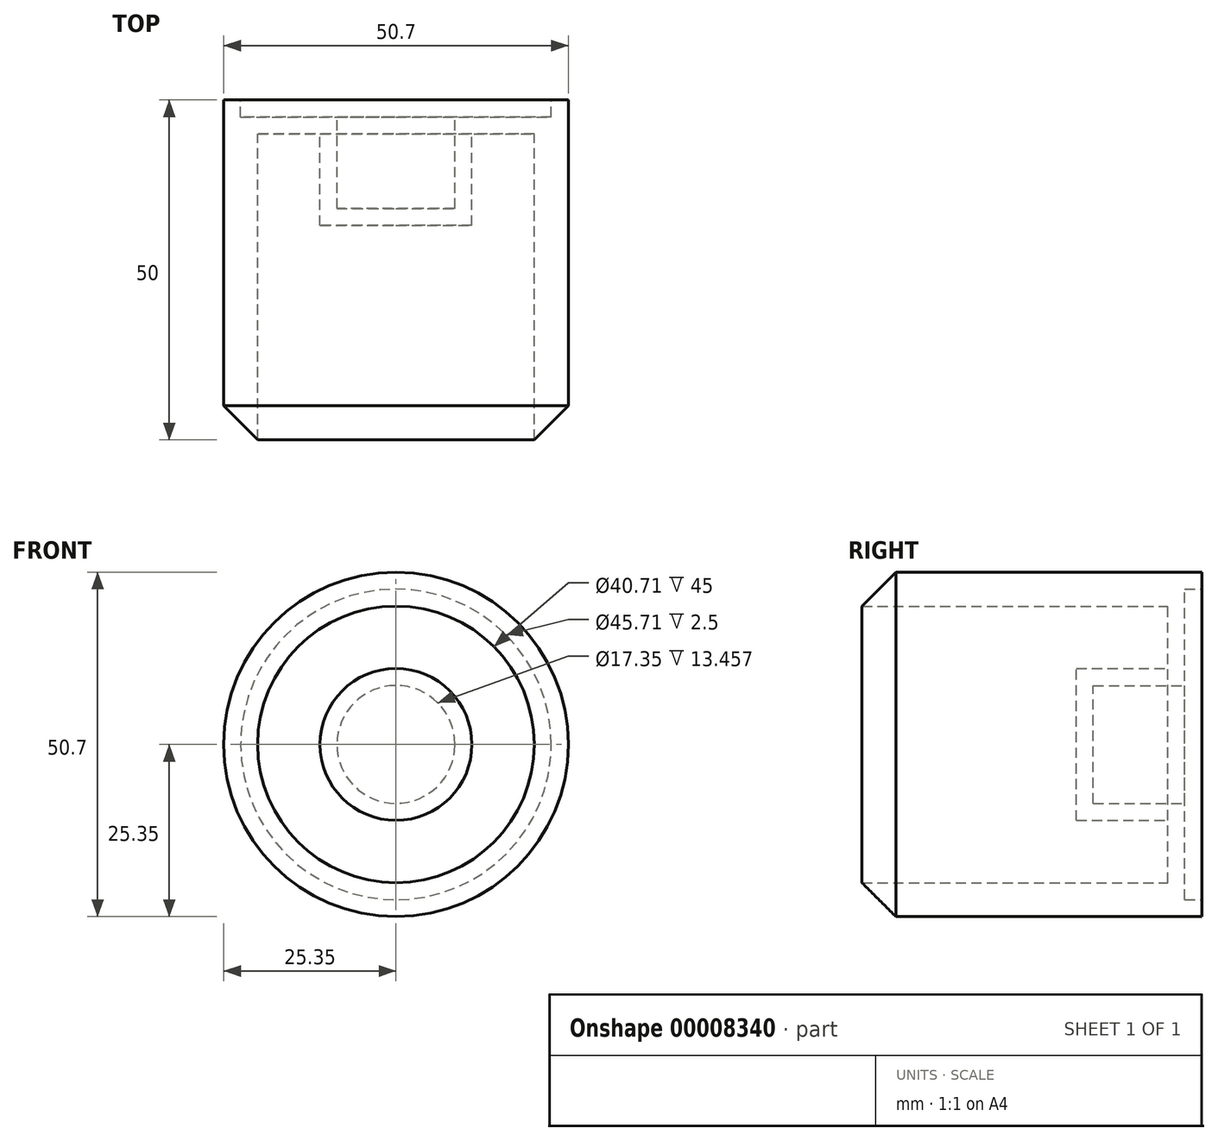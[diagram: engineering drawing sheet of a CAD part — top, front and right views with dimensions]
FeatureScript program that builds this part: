
annotation { "Feature Type Name" : "Feature", "Feature Type Description" : "" }
export const myFeature = defineFeature(function(context is Context, id is Id, definition is map)
    precondition{}
    {
        {
            var Q0;
            Q0=qCreatedBy(makeId("Front.planeOp"),FACE);
            var sketch = newSketch(context, id + "F0", { "sketchPlane" : qUnion([Q0])});
            skCircle(sketch, "E0", {"center": v(0, 0) * mm, "radius": 25.35 * mm});
            skSolve(sketch);
        }
        {
            var Q0;
            Q0=makeQuery(id+"F0.imprint","IMPRINT",FACE,{"disambiguationData":[TD([[makeQuery(id+"F0.imprint","IMPRINT",EDGE,{"derivedFrom":sQuery(id+"F0.wireOp",EDGE,"E0")}),1.0]])]});
            extrude(context, id + "F1", {"entities" : qUnion([Q0]), "depth" : 50 * mm});
        }
        {
            var Q0;
            Q0=makeQuery(id+"F1.opExtrude","CAP_FACE",FACE,{"disambiguationData":[OSD([sQuery(id+"F0.wireOp",EDGE,"E0")])],"isStart":false});
            shell(context, id + "F2", {"entities" : qUnion([Q0]), "thickness" : 5 * mm});
        }
        {
            var Q0;
            Q0=makeQuery(id+"F0.imprint","IMPRINT",FACE,{"disambiguationData":[TD([[makeQuery(id+"F0.imprint","IMPRINT",EDGE,{"derivedFrom":sQuery(id+"F0.wireOp",EDGE,"E0")}),1.0]])]});
            var sketch = newSketch(context, id + "F3", { "sketchPlane" : qUnion([Q0])});
            skCircle(sketch, "E1", {"center": v(0, 0) * mm, "radius": 11.18 * mm});
            skSolve(sketch);
        }
        {
            var Q0;
            Q0=makeQuery(id+"F3.imprint","IMPRINT",FACE,{"disambiguationData":[TD([[makeQuery(id+"F3.imprint","IMPRINT",EDGE,{"derivedFrom":sQuery(id+"F3.wireOp",EDGE,"E1")}),1.0]])]});
            extrude(context, id + "F4", {"entities" : qUnion([Q0]), "operationType" : NewBodyOperationType.ADD, "depth" : 18.46 * mm});
        }
        {
            var Q0;
            Q0=makeQuery(id+"F1.opExtrude","CAP_FACE",FACE,{"disambiguationData":[OSD([sQuery(id+"F0.wireOp",EDGE,"E0")])],"isStart":true});
            shell(context, id + "F5", {"entities" : qUnion([Q0]), "thickness" : 2.5 * mm});
        }
        {
            var Q0;
            Q0=makeQuery(id+"F1.opExtrude","CAP_EDGE",EDGE,{"disambiguationData":[OSD([sQuery(id+"F0.wireOp",EDGE,"E0")])],"isStart":false});
            chamfer(context, id + "F6", {"entities" : qUnion([Q0]), "width" : 5 * mm, "tangentPropagation" : true});
        }
    });
